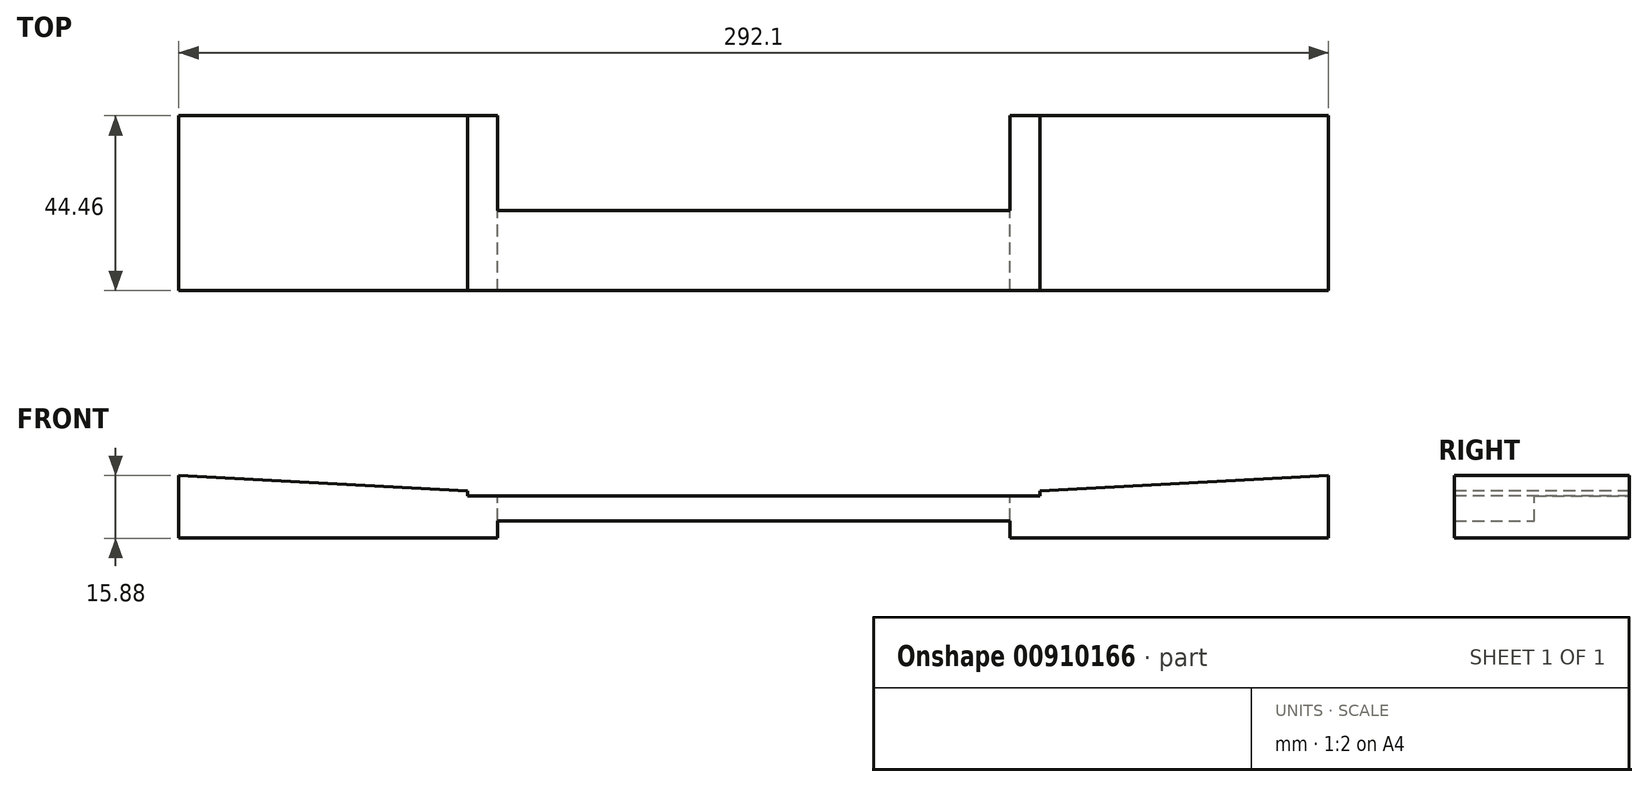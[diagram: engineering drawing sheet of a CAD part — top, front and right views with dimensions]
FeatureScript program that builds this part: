
annotation { "Feature Type Name" : "Feature", "Feature Type Description" : "" }
export const myFeature = defineFeature(function(context is Context, id is Id, definition is map)
    precondition{}
    {
        {
            var Q0;
            Q0=qCreatedBy(makeId("Top.planeOp"),FACE);
            var sketch = newSketch(context, id + "F0", { "sketchPlane" : qUnion([Q0])});
            skLineSegment(sketch, "E0.bottom", {"start": v(146.05, -22.23) * mm, "end": v(-146.05, -22.22) * mm});
            skLineSegment(sketch, "E0.top", {"start": v(146.05, 22.22) * mm, "end": v(-146.05, 22.23) * mm});
            skLineSegment(sketch, "E0.left", {"start": v(146.05, -22.23) * mm, "end": v(146.05, 22.23) * mm});
            skLineSegment(sketch, "E0.right", {"start": v(-146.05, -22.23) * mm, "end": v(-146.05, 22.23) * mm});
            skLineSegment(sketch, "E1", {"start": v(0, 22.23) * mm, "end": v(0, -22.23) * mm, "construction": true});
            skLineSegment(sketch, "E2", {"start": v(-146.05, 0) * mm, "end": v(146.05, 0) * mm, "construction": true});
            skPoint(sketch, "E3", {"position": v(0, 0) * mm});
            skSolve(sketch);
        }
        {
            var Q0;
            Q0 = qSketchRegion(id + "F0", true);
            extrude(context, id + "F1", {"entities" : qUnion([Q0]), "depth" : 6.35 * mm, "offsetDistance" : 25 * mm});
        }
        {
            var Q0;
            Q0=makeQuery(id+"F1.opExtrude","CAP_FACE",FACE,{"disambiguationData":[OSD([sQuery(id+"F0.wireOp",EDGE,"E0.bottom"),sQuery(id+"F0.wireOp",EDGE,"E0.top"),sQuery(id+"F0.wireOp",EDGE,"E0.left"),sQuery(id+"F0.wireOp",EDGE,"E0.right")])],"isStart":false});
            var sketch = newSketch(context, id + "F2", { "sketchPlane" : qUnion([Q0])});
            skLineSegment(sketch, "E4.bottom", {"start": v(65.09, -1.9) * mm, "end": v(-65.09, -1.9) * mm});
            skLineSegment(sketch, "E4.top", {"start": v(65.09, 22.23) * mm, "end": v(-65.09, 22.22) * mm});
            skLineSegment(sketch, "E4.left", {"start": v(65.09, -1.9) * mm, "end": v(65.09, 22.23) * mm});
            skLineSegment(sketch, "E4.right", {"start": v(-65.09, -1.9) * mm, "end": v(-65.09, 22.22) * mm});
            skPoint(sketch, "E4.middle", {"position": v(0, 10.16) * mm});
            skSolve(sketch);
        }
        {
            var Q0;
            Q0 = qSketchRegion(id + "F2", true);
            extrude(context, id + "F3", {"entities" : qUnion([Q0]), "operationType" : NewBodyOperationType.REMOVE, "endBound" : BoundingType.THROUGH_ALL, "oppositeDirection" : true, "depth" : 25.4 * mm, "offsetDistance" : 25.4 * mm});
        }
        {
            var Q0;
            Q0=makeQuery(id+"F1.opExtrude","CAP_FACE",FACE,{"disambiguationData":[OSD([sQuery(id+"F0.wireOp",EDGE,"E0.bottom"),sQuery(id+"F0.wireOp",EDGE,"E0.top"),sQuery(id+"F0.wireOp",EDGE,"E0.left"),sQuery(id+"F0.wireOp",EDGE,"E0.right")])],"isStart":true});
            var sketch = newSketch(context, id + "F4", { "sketchPlane" : qUnion([Q0])});
            skLineSegment(sketch, "E5.bottom", {"start": v(-146.05, 22.23) * mm, "end": v(-65.09, 22.23) * mm});
            skLineSegment(sketch, "E5.top", {"start": v(-146.05, -22.23) * mm, "end": v(-65.09, -22.23) * mm});
            skLineSegment(sketch, "E5.left", {"start": v(-146.05, 22.23) * mm, "end": v(-146.05, -22.23) * mm});
            skLineSegment(sketch, "E5.right", {"start": v(-65.09, 22.23) * mm, "end": v(-65.09, -22.23) * mm});
            skLineSegment(sketch, "E6.bottom", {"start": v(146.05, 22.23) * mm, "end": v(65.09, 22.23) * mm});
            skLineSegment(sketch, "E6.top", {"start": v(146.05, -22.22) * mm, "end": v(65.09, -22.22) * mm});
            skLineSegment(sketch, "E6.left", {"start": v(146.05, 22.23) * mm, "end": v(146.05, -22.22) * mm});
            skLineSegment(sketch, "E6.right", {"start": v(65.09, 22.23) * mm, "end": v(65.09, -22.22) * mm});
            skSolve(sketch);
        }
        {
            var Q0;
            Q0 = qSketchRegion(id + "F4", true);
            extrude(context, id + "F5", {"entities" : qUnion([Q0]), "operationType" : NewBodyOperationType.ADD, "depth" : 4.32 * mm, "offsetDistance" : 25.4 * mm});
        }
        {
            var Q0;
            Q0=makeQuery(id+"F5.boolean.opBoolean","MERGE",FACE,{"derivedFrom":[makeQuery(id+"F1.opExtrude","SWEPT_FACE",FACE,{"disambiguationData":[OSD([sQuery(id+"F0.wireOp",EDGE,"E0.bottom")])]}),makeQuery(id+"F5.opExtrude","SWEPT_FACE",FACE,{"disambiguationData":[OSD([sQuery(id+"F4.wireOp",EDGE,"E5.bottom")])]}),makeQuery(id+"F5.opExtrude","SWEPT_FACE",FACE,{"disambiguationData":[OSD([sQuery(id+"F4.wireOp",EDGE,"E6.bottom")])]})]});
            var sketch = newSketch(context, id + "F6", { "sketchPlane" : qUnion([Q0])});
            skLineSegment(sketch, "E7", {"start": v(-146.05, 6.35) * mm, "end": v(-146.05, 11.56) * mm});
            skLineSegment(sketch, "E8", {"start": v(-146.05, 11.56) * mm, "end": v(-72.7, 7.71) * mm});
            skLineSegment(sketch, "E9", {"start": v(-72.7, 7.71) * mm, "end": v(-72.7, 6.35) * mm});
            skLineSegment(sketch, "E10", {"start": v(-72.7, 7.71) * mm, "end": v(-146.05, 7.71) * mm, "construction": true});
            skLineSegment(sketch, "E11", {"start": v(0, 0) * mm, "end": v(0, 6.35) * mm, "construction": true});
            skLineSegment(sketch, "E12.MirrorCS", {"start": v(72.7, 7.71) * mm, "end": v(72.7, 6.35) * mm});
            skLineSegment(sketch, "E13.MirrorCS", {"start": v(146.05, 6.35) * mm, "end": v(146.05, 11.56) * mm});
            skLineSegment(sketch, "E14.MirrorCS", {"start": v(146.05, 11.56) * mm, "end": v(72.7, 7.71) * mm});
            skLineSegment(sketch, "E15.MirrorCS", {"start": v(72.7, 7.71) * mm, "end": v(146.05, 7.71) * mm, "construction": true});
            skSolve(sketch);
        }
        {
            var Q0;
            Q0 = qSketchRegion(id + "F6", true);
            var Q1;
            {var subQ0=sQuery(id+"F6.wireOp",EDGE,"E7");Q1=makeQuery(id+"F6.imprint","IMPRINT",FACE,{"disambiguationData":[TD([[makeQuery(id+"F6.imprint","IMPRINT",EDGE,{"derivedFrom":subQ0}),-1.0]])]});}
            var Q2;
            {var subQ0=sQuery(id+"F6.wireOp",EDGE,"E12.MirrorCS");Q2=makeQuery(id+"F6.imprint","IMPRINT",FACE,{"disambiguationData":[TD([[makeQuery(id+"F6.imprint","IMPRINT",EDGE,{"derivedFrom":subQ0}),1.0]])]});}
            var Q3;
            {var subQ1=sQuery(id+"F0.wireOp",EDGE,"E0.left");var subQ2=sQuery(id+"F0.wireOp",EDGE,"E0.top");Q3=makeQuery(id+"F5.boolean.opBoolean","MERGE",FACE,{"derivedFrom":[makeQuery(id+"F3.boolean.opBoolean","SPLIT",FACE,{"disambiguationData":[TD([makeQuery(id+"F1.opExtrude","SWEPT_FACE",FACE,{"disambiguationData":[OSD([subQ1])]})])],"derivedFrom":makeQuery(id+"F1.opExtrude","SWEPT_FACE",FACE,{"disambiguationData":[OSD([subQ2])]})}),makeQuery(id+"F5.opExtrude","SWEPT_FACE",FACE,{"disambiguationData":[OSD([sQuery(id+"F4.wireOp",EDGE,"E6.top")])]})]});}
            extrude(context, id + "F7", {"entities" : qUnion([Q0, Q1, Q2]), "operationType" : NewBodyOperationType.ADD, "endBound" : BoundingType.UP_TO_SURFACE, "oppositeDirection" : true, "depth" : 25.4 * mm, "endBoundEntityFace" : qUnion([Q3]), "offsetDistance" : 25.4 * mm});
        }
    });
